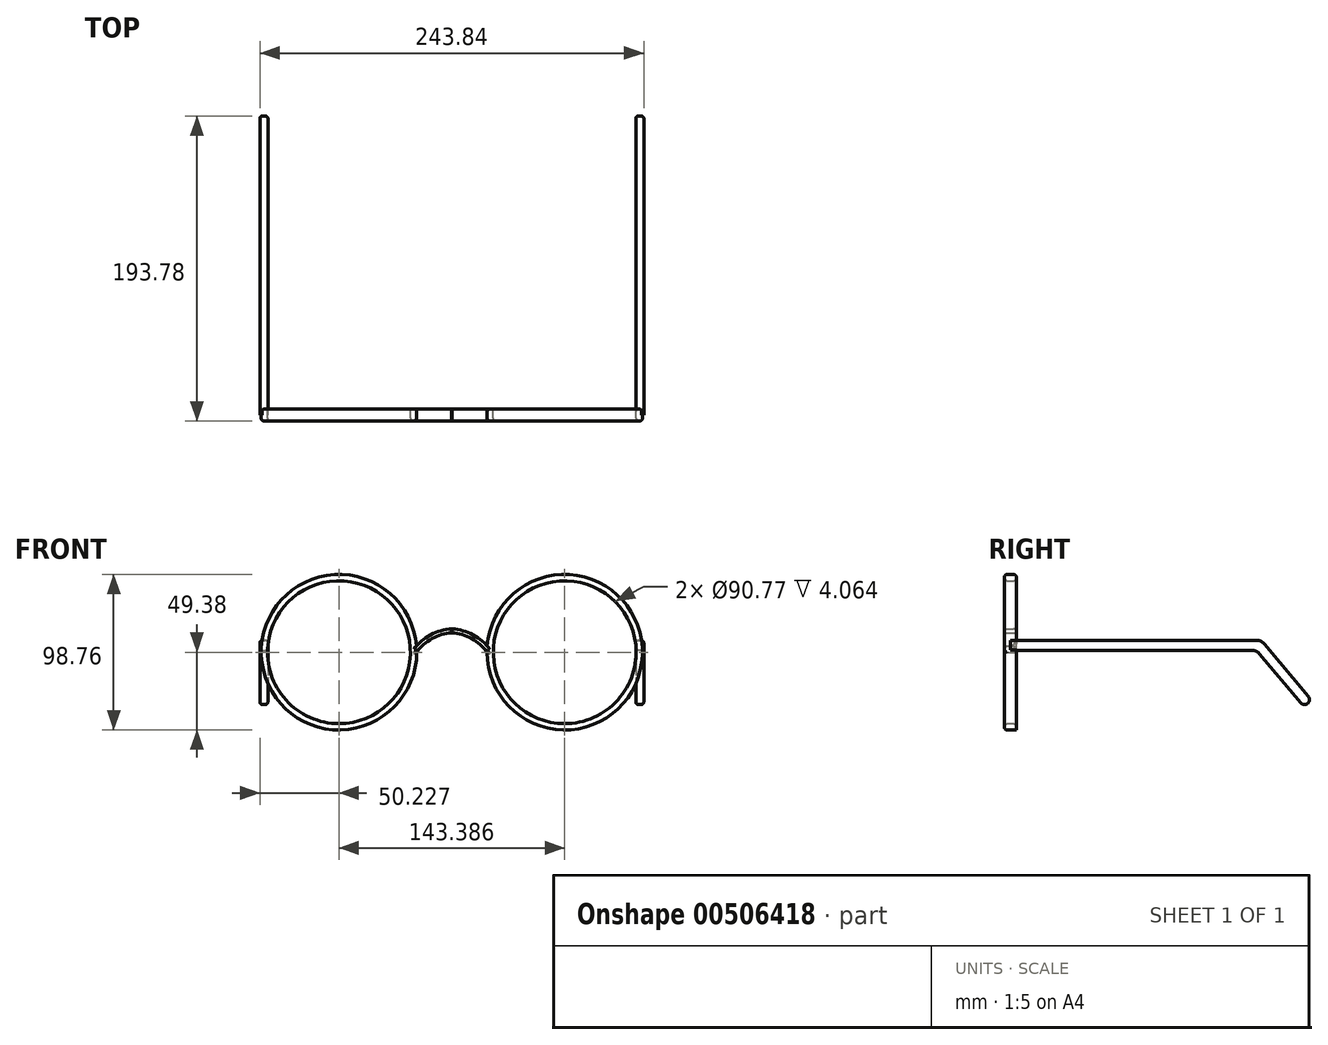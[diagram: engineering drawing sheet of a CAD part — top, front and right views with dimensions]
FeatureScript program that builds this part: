
annotation { "Feature Type Name" : "Feature", "Feature Type Description" : "" }
export const myFeature = defineFeature(function(context is Context, id is Id, definition is map)
    precondition{}
    {
        {
            var Q0;
            Q0=qCreatedBy(makeId("Front.planeOp"),FACE);
            var sketch = newSketch(context, id + "F0", { "sketchPlane" : qUnion([Q0])});
            skCircle(sketch, "E0", {"center": v(71.7, 0) * mm, "radius": 49.38 * mm});
            skCircle(sketch, "E1.0", {"center": v(71.7, 0) * mm, "radius": 45.39 * mm});
            skArc(sketch, "E2", {"start": v(22.3, 0) * mm, "mid": v(12.57, 8.68) * mm, "end": v(0, 12.2) * mm});
            skArc(sketch, "E3.0", {"start": v(22.46, 3.91) * mm, "mid": v(12.4, 11.62) * mm, "end": v(0.11, 14.73) * mm});
            skLineSegment(sketch, "E4", {"start": v(0.11, 14.73) * mm, "end": v(0, 12.2) * mm});
            skSolve(sketch);
        }
        {
            var Q0;
            Q0 = qSketchRegion(id + "F0", true);
            extrude(context, id + "F1", {"entities" : qUnion([Q0]), "endBound" : BoundingType.SYMMETRIC, "depth" : 7.62 * mm});
        }
        {
            var Q0;
            Q0=qCreatedBy(makeId("Right.planeOp"),FACE);
            cPlane(context, id + "F2", {"entities" : qUnion([Q0]), "cplaneType" : CPlaneType.OFFSET, "offset" : 119.38 * mm, "width" : 152.4 * mm, "height" : 152.4 * mm});
        }
        {
            var Q0;
            Q0=qCreatedBy(id+"F2.planeOp",FACE);
            var sketch = newSketch(context, id + "F3", { "sketchPlane" : qUnion([Q0])});
            skLineSegment(sketch, "E5", {"start": v(0, 7.6) * mm, "end": v(156.32, 7.6) * mm});
            skLineSegment(sketch, "E6", {"start": v(161.18, 5.33) * mm, "end": v(189.23, -28.06) * mm});
            skLineSegment(sketch, "E7.0", {"start": v(158.22, -1.02) * mm, "end": v(184.36, -32.15) * mm});
            skLineSegment(sketch, "E7.1", {"start": v(0, 1.25) * mm, "end": v(153.36, 1.25) * mm});
            skArc(sketch, "E8", {"start": v(189.23, -28.06) * mm, "mid": v(188.84, -32.53) * mm, "end": v(184.36, -32.15) * mm});
            skLineSegment(sketch, "E9", {"start": v(0, 1.25) * mm, "end": v(0, 7.6) * mm});
            skPoint(sketch, "E10.visualSharp", {"position": v(156.32, 1.25) * mm});
            skArc(sketch, "E10.filletArc", {"start": v(158.22, -1.02) * mm, "mid": v(156.04, 0.65) * mm, "end": v(153.36, 1.25) * mm});
            skPoint(sketch, "E11.visualSharp", {"position": v(159.27, 7.6) * mm});
            skArc(sketch, "E11.filletArc", {"start": v(161.18, 5.33) * mm, "mid": v(159, 7) * mm, "end": v(156.32, 7.6) * mm});
            skSolve(sketch);
        }
        {
            var Q0;
            Q0 = qSketchRegion(id + "F3", true);
            extrude(context, id + "F4", {"entities" : qUnion([Q0]), "operationType" : NewBodyOperationType.ADD, "endBound" : BoundingType.SYMMETRIC, "depth" : 5.08 * mm});
        }
        {
            var Q0;
            Q0=makeQuery(id+"F4.opExtrude","CAP_EDGE",EDGE,{"disambiguationData":[OSD([sQuery(id+"F3.wireOp",EDGE,"E5")])],"isStart":false});
            var Q1;
            Q1=makeQuery(id+"F4.opExtrude","CAP_EDGE",EDGE,{"disambiguationData":[OSD([sQuery(id+"F3.wireOp",EDGE,"E7.1")])],"isStart":false});
            var Q2;
            Q2=makeQuery(id+"F4.opExtrude","CAP_EDGE",EDGE,{"disambiguationData":[OSD([sQuery(id+"F3.wireOp",EDGE,"E5")])],"isStart":true});
            var Q3;
            Q3=makeQuery(id+"F4.opExtrude","CAP_EDGE",EDGE,{"disambiguationData":[OSD([sQuery(id+"F3.wireOp",EDGE,"E7.1")])],"isStart":true});
            var Q4;
            Q4=makeQuery(id+"F4.opExtrude","CAP_EDGE",EDGE,{"disambiguationData":[OSD([sQuery(id+"F3.wireOp",EDGE,"E6")])],"isStart":true});
            var Q5;
            Q5=makeQuery(id+"F4.opExtrude","CAP_EDGE",EDGE,{"disambiguationData":[OSD([sQuery(id+"F3.wireOp",EDGE,"E7.0")])],"isStart":false});
            var Q6;
            Q6=makeQuery(id+"F4.opExtrude","CAP_EDGE",EDGE,{"disambiguationData":[OSD([sQuery(id+"F3.wireOp",EDGE,"E8")])],"isStart":false});
            var Q7;
            Q7=makeQuery(id+"F4.opExtrude","CAP_EDGE",EDGE,{"disambiguationData":[OSD([sQuery(id+"F3.wireOp",EDGE,"E8")])],"isStart":true});
            var Q8;
            Q8=makeQuery(id+"F4.opExtrude","CAP_EDGE",EDGE,{"disambiguationData":[OSD([sQuery(id+"F3.wireOp",EDGE,"E11.filletArc")])],"isStart":false});
            var Q9;
            Q9=makeQuery(id+"F4.opExtrude","CAP_EDGE",EDGE,{"disambiguationData":[OSD([sQuery(id+"F3.wireOp",EDGE,"E11.filletArc")])],"isStart":true});
            var Q10;
            Q10=makeQuery(id+"F4.opExtrude","CAP_EDGE",EDGE,{"disambiguationData":[OSD([sQuery(id+"F3.wireOp",EDGE,"E10.filletArc")])],"isStart":false});
            fillet(context, id + "F5", {"entities" : qUnion([Q0, Q1, Q2, Q3, Q4, Q5, Q6, Q7, Q8, Q9, Q10]), "radius" : 1.78 * mm, "tangentPropagation" : true, "allowEdgeOverflow" : false});
        }
        {
            var Q0;
            Q0=makeQuery(id+"F1.opExtrude","CAP_EDGE",EDGE,{"disambiguationData":[OSD([sQuery(id+"F0.wireOp",EDGE,"E2")])],"isStart":false});
            var Q1;
            Q1=makeQuery(id+"F1.opExtrude","CAP_EDGE",EDGE,{"disambiguationData":[OSD([sQuery(id+"F0.wireOp",EDGE,"E3.0")])],"isStart":true});
            var Q2;
            Q2=makeQuery(id+"F1.opExtrude","CAP_EDGE",EDGE,{"disambiguationData":[OSD([sQuery(id+"F0.wireOp",EDGE,"E1.0")])],"isStart":false});
            var Q3;
            Q3=makeQuery(id+"F1.opExtrude","CAP_EDGE",EDGE,{"disambiguationData":[OSD([sQuery(id+"F0.wireOp",EDGE,"E0")])],"isStart":false});
            var Q4;
            {var subQ0=sQuery(id+"F0.wireOp",EDGE,"E0");var subQ1=sQuery(id+"F0.wireOp",EDGE,"E3.0");Q4=makeQuery(id+"F4.boolean.opBoolean","SPLIT",EDGE,{"disambiguationData":[TD([makeQuery(id+"F1.opExtrude","SWEPT_FACE",FACE,{"disambiguationData":[OSD([subQ1])]})])],"derivedFrom":makeQuery(id+"F1.opExtrude","CAP_EDGE",EDGE,{"disambiguationData":[OSD([subQ0])],"isStart":true})});}
            var Q5;
            Q5=makeQuery(id+"F1.opExtrude","CAP_EDGE",EDGE,{"disambiguationData":[OSD([sQuery(id+"F0.wireOp",EDGE,"E1.0")])],"isStart":true});
            fillet(context, id + "F6", {"entities" : qUnion([Q0, Q1, Q2, Q3, Q4, Q5]), "radius" : 1.78 * mm, "tangentPropagation" : true, "allowEdgeOverflow" : false});
        }
        {
            var Q0;
            Q0=makeQuery(id+"F1.opExtrude","SWEPT_BODY",BODY,{"disambiguationData":[OSD([sQuery(id+"F0.wireOp",EDGE,"E0"),sQuery(id+"F0.wireOp",EDGE,"E1.0"),sQuery(id+"F0.wireOp",EDGE,"E2"),sQuery(id+"F0.wireOp",EDGE,"E3.0"),sQuery(id+"F0.wireOp",EDGE,"E4")])]});
            var Q1;
            Q1=qCreatedBy(makeId("Right.planeOp"),FACE);
            mirror(context, id + "F7", {"entities" : qUnion([Q0]), "mirrorPlane" : qUnion([Q1])});
        }
    });
